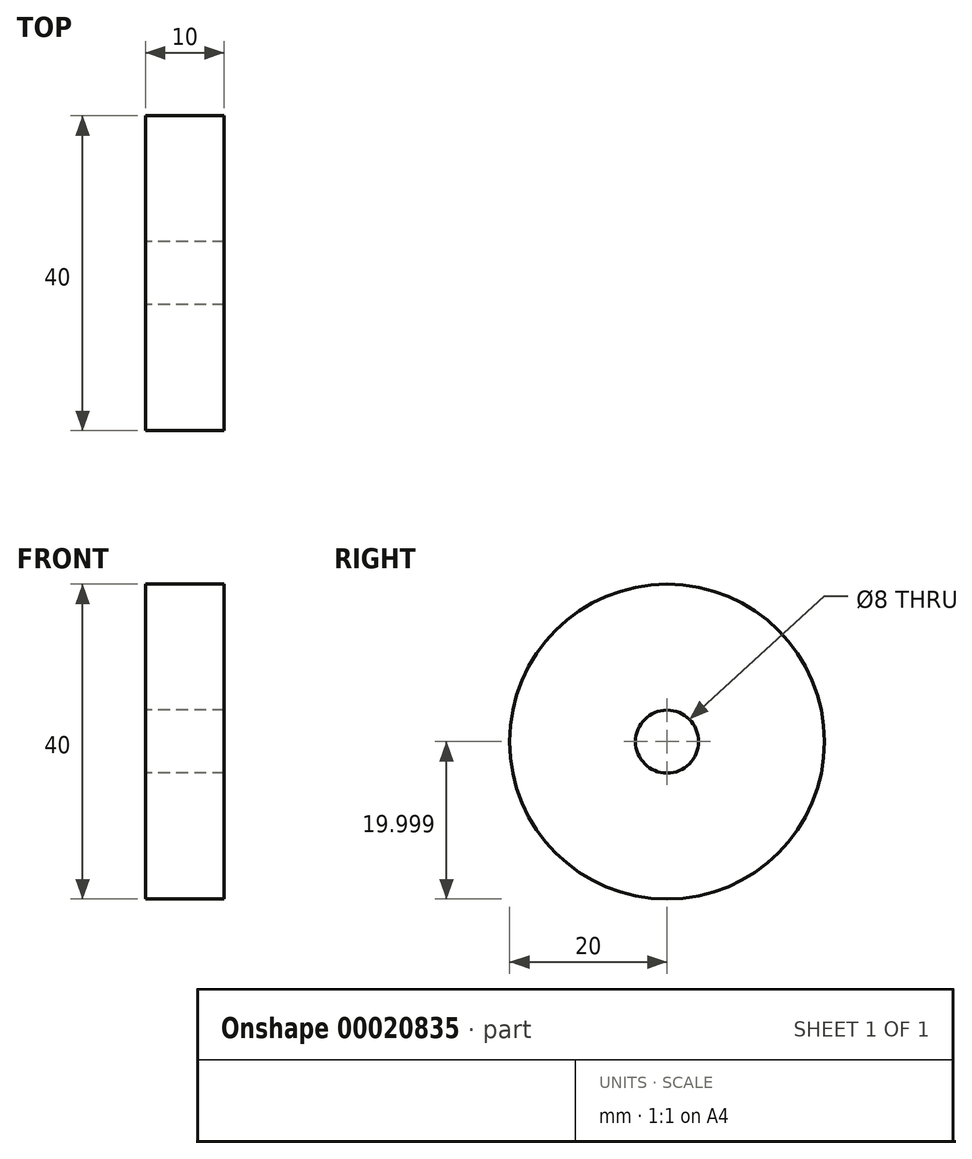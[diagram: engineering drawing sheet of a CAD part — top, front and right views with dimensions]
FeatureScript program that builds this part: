
annotation { "Feature Type Name" : "Feature", "Feature Type Description" : "" }
export const myFeature = defineFeature(function(context is Context, id is Id, definition is map)
    precondition{}
    {
        {
            var Q0;
            Q0=qCreatedBy(makeId("Right.planeOp"),FACE);
            var sketch = newSketch(context, id + "F0", { "sketchPlane" : qUnion([Q0])});
            skCircle(sketch, "E0", {"center": v(-29.35, 37.27) * mm, "radius": 20 * mm});
            skCircle(sketch, "E1", {"center": v(-29.35, 37.27) * mm, "radius": 4 * mm});
            skSolve(sketch);
        }
        {
            var Q0;
            Q0 = qSketchRegion(id + "F0", true);
            extrude(context, id + "F1", {"entities" : qUnion([Q0]), "depth" : 10 * mm});
        }
    });
